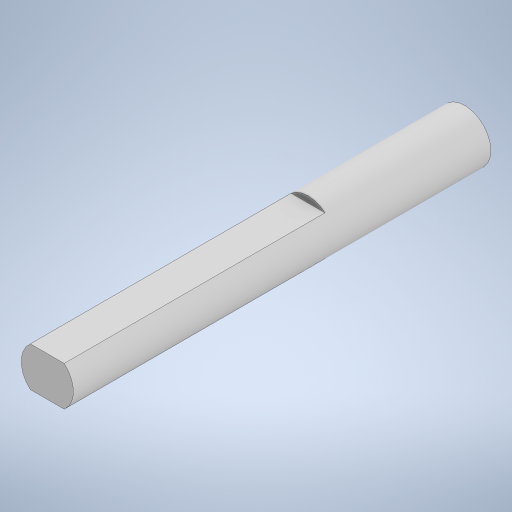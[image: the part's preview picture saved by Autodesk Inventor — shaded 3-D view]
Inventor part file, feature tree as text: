
AUTODESK INVENTOR PART (.ipt)
format: ipt  version: 2024 (Build 280153000, 153)  size: 225,280 bytes
history: native  units: in
note: dims shown in document units (in); Inventor stores cm internally (conversion verified against a paired STEP export)
features: extrude x2, sketch x2
ambient origin geometry x8: Origin, YZ Plane, XZ Plane, XY Plane, X Axis, Y Axis, Z Axis, Center Point
bodies: Solid1 (feature_tree)
feature tree (4):
  extrude  "Extrusion1"  Depth=0.3937in TaperAngle=0.0deg
  extrude  "Extrusion2"  Depth=0.9843in
  sketch  "Sketch1"  dims[d0=0.1969in d1=0.3937in d2=0.0in]
  sketch  "Sketch2"  dims[d3=0.0748in d4=0.0748in d5=0.1969in d6=0.0in d7=0.9843in d8=0.0in]
